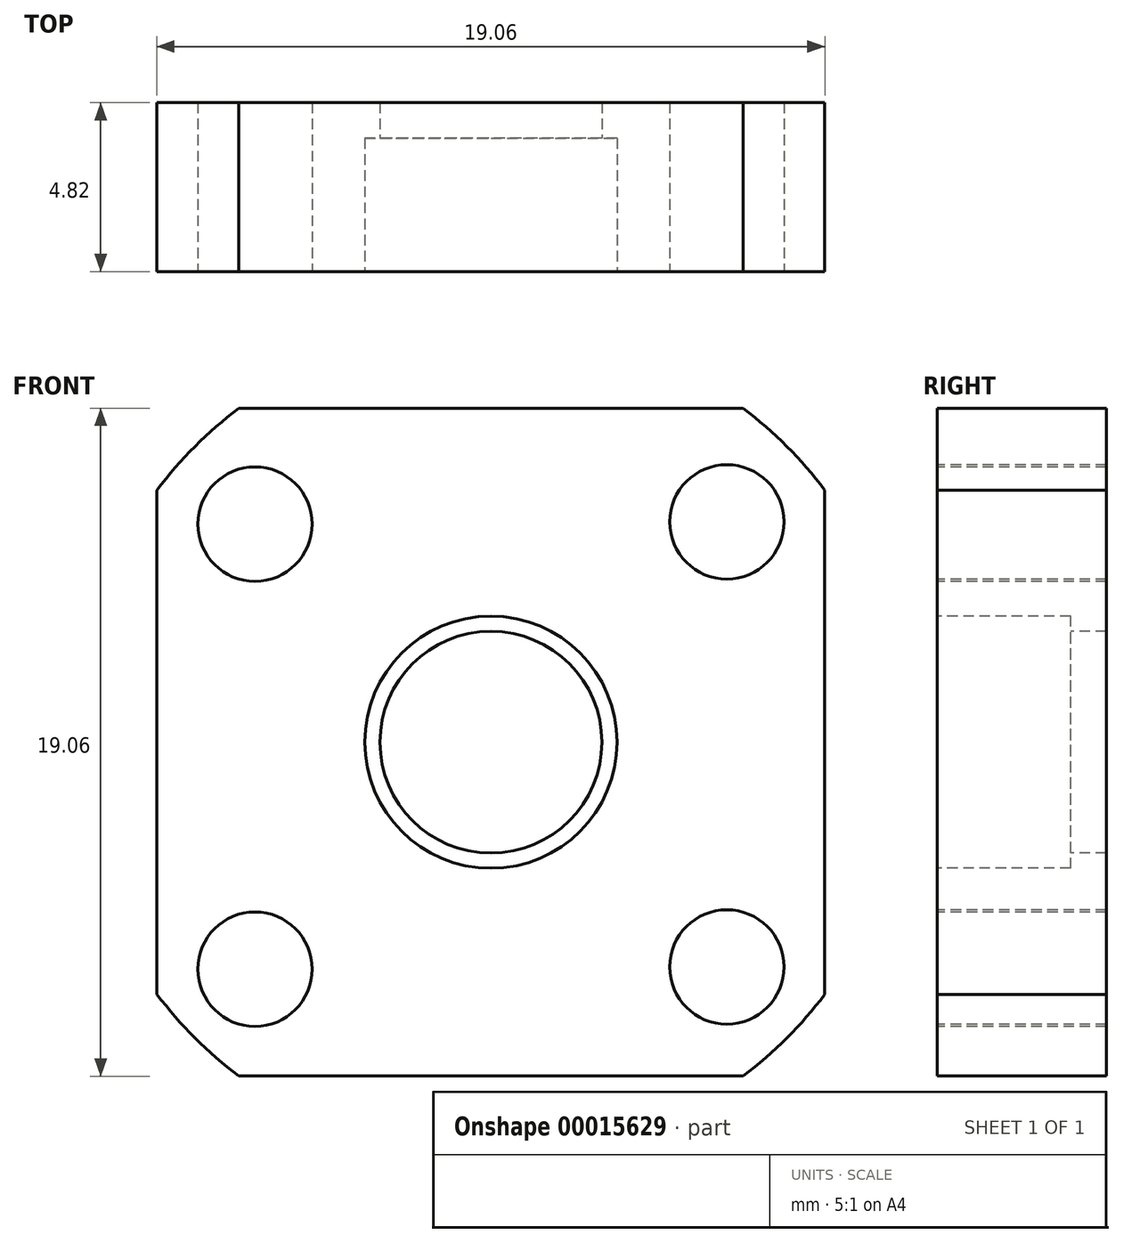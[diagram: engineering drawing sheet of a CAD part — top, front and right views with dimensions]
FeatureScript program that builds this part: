
annotation { "Feature Type Name" : "Feature", "Feature Type Description" : "" }
export const myFeature = defineFeature(function(context is Context, id is Id, definition is map)
    precondition{}
    {
        {
            var Q0;
            Q0=qCreatedBy(makeId("Front.planeOp"),FACE);
            var sketch = newSketch(context, id + "F0", { "sketchPlane" : qUnion([Q0])});
            skLineSegment(sketch, "E0.bottom", {"start": v(-9.53, 9.53) * mm, "end": v(9.52, 9.53) * mm});
            skLineSegment(sketch, "E0.top", {"start": v(-9.53, -9.53) * mm, "end": v(9.53, -9.53) * mm});
            skLineSegment(sketch, "E0.left", {"start": v(-9.53, 9.53) * mm, "end": v(-9.53, -9.53) * mm});
            skLineSegment(sketch, "E0.right", {"start": v(9.52, 9.53) * mm, "end": v(9.53, -9.53) * mm});
            skSolve(sketch);
        }
        {
            var Q0;
            Q0=makeQuery(id+"F0.imprint","IMPRINT",FACE,{"disambiguationData":[TD([[makeQuery(id+"F0.imprint","IMPRINT",EDGE,{"derivedFrom":sQuery(id+"F0.wireOp",EDGE,"E0.bottom")}),-1.0]])]});
            extrude(context, id + "F1", {"entities" : qUnion([Q0]), "endBound" : BoundingType.SYMMETRIC, "depth" : 4.83 * mm});
        }
        {
            var Q0;
            Q0=makeQuery(id+"F1.opExtrude","CAP_FACE",FACE,{"disambiguationData":[OSD([sQuery(id+"F0.wireOp",EDGE,"E0.bottom"),sQuery(id+"F0.wireOp",EDGE,"E0.top"),sQuery(id+"F0.wireOp",EDGE,"E0.left"),sQuery(id+"F0.wireOp",EDGE,"E0.right")])],"isStart":false});
            var sketch = newSketch(context, id + "F2", { "sketchPlane" : qUnion([Q0])});
            skCircle(sketch, "E1", {"center": v(0, 0) * mm, "radius": 11.94 * mm});
            skCircle(sketch, "E2", {"center": v(0, 0) * mm, "radius": 20.78 * mm});
            skSolve(sketch);
        }
        {
            var Q0;
            Q0 = qSketchRegion(id + "F2", true);
            extrude(context, id + "F3", {"entities" : qUnion([Q0]), "operationType" : NewBodyOperationType.REMOVE, "endBound" : BoundingType.THROUGH_ALL, "oppositeDirection" : true, "depth" : 25.4 * mm});
        }
        {
            var Q0;
            Q0=makeQuery(id+"F1.opExtrude","CAP_FACE",FACE,{"disambiguationData":[OSD([sQuery(id+"F0.wireOp",EDGE,"E0.bottom"),sQuery(id+"F0.wireOp",EDGE,"E0.top"),sQuery(id+"F0.wireOp",EDGE,"E0.left"),sQuery(id+"F0.wireOp",EDGE,"E0.right")])],"isStart":false});
            var sketch = newSketch(context, id + "F4", { "sketchPlane" : qUnion([Q0])});
            skCircle(sketch, "E3", {"center": v(0, 0) * mm, "radius": 3.17 * mm});
            skSolve(sketch);
        }
        {
            var Q0;
            Q0 = qSketchRegion(id + "F4", true);
            extrude(context, id + "F5", {"entities" : qUnion([Q0]), "operationType" : NewBodyOperationType.REMOVE, "endBound" : BoundingType.THROUGH_ALL, "oppositeDirection" : true, "depth" : 3.8 * mm});
        }
        {
            var Q0;
            Q0=makeQuery(id+"F1.opExtrude","CAP_FACE",FACE,{"disambiguationData":[OSD([sQuery(id+"F0.wireOp",EDGE,"E0.bottom"),sQuery(id+"F0.wireOp",EDGE,"E0.top"),sQuery(id+"F0.wireOp",EDGE,"E0.left"),sQuery(id+"F0.wireOp",EDGE,"E0.right")])],"isStart":false});
            var sketch = newSketch(context, id + "F6", { "sketchPlane" : qUnion([Q0])});
            skCircle(sketch, "E4", {"center": v(0, 0) * mm, "radius": 3.6 * mm});
            skSolve(sketch);
        }
        {
            var Q0;
            Q0 = qSketchRegion(id + "F6", true);
            extrude(context, id + "F7", {"entities" : qUnion([Q0]), "operationType" : NewBodyOperationType.REMOVE, "oppositeDirection" : true, "depth" : 3.8 * mm});
        }
        {
            var Q0;
            Q0=makeQuery(id+"F1.opExtrude","CAP_FACE",FACE,{"disambiguationData":[OSD([sQuery(id+"F0.wireOp",EDGE,"E0.bottom"),sQuery(id+"F0.wireOp",EDGE,"E0.top"),sQuery(id+"F0.wireOp",EDGE,"E0.left"),sQuery(id+"F0.wireOp",EDGE,"E0.right")])],"isStart":false});
            var sketch = newSketch(context, id + "F8", { "sketchPlane" : qUnion([Q0])});
            skCircle(sketch, "E5", {"center": v(-6.73, 6.22) * mm, "radius": 1.63 * mm});
            skCircle(sketch, "E6.0.1.0", {"center": v(-6.73, -6.48) * mm, "radius": 1.63 * mm});
            skCircle(sketch, "E6.1.0.0", {"center": v(6.73, 6.29) * mm, "radius": 1.63 * mm});
            skCircle(sketch, "E6.1.1.0", {"center": v(6.73, -6.41) * mm, "radius": 1.63 * mm});
            skLineSegment(sketch, "E6.direction1", {"start": v(-6.73, 6.22) * mm, "end": v(6.73, 6.29) * mm, "construction": true});
            skLineSegment(sketch, "E6.direction2", {"start": v(-6.73, 6.22) * mm, "end": v(-6.73, -6.48) * mm, "construction": true});
            skSolve(sketch);
        }
        {
            var Q0;
            Q0 = qSketchRegion(id + "F8", true);
            extrude(context, id + "F9", {"entities" : qUnion([Q0]), "operationType" : NewBodyOperationType.REMOVE, "endBound" : BoundingType.THROUGH_ALL, "oppositeDirection" : true, "depth" : 25.4 * mm});
        }
    });
